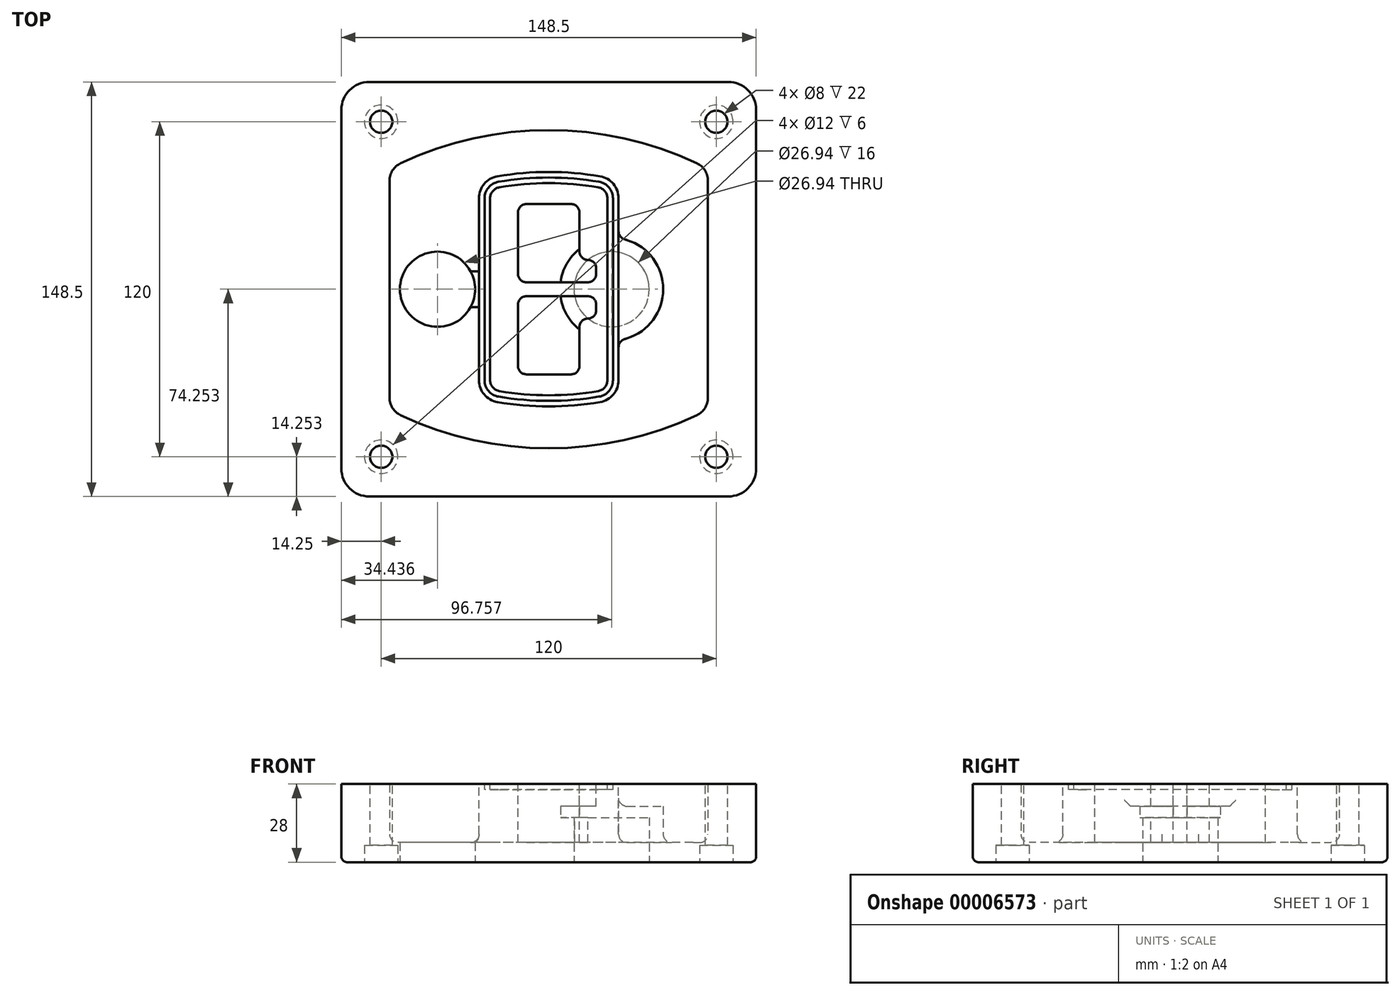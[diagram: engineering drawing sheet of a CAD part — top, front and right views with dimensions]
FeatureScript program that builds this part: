
annotation { "Feature Type Name" : "Feature", "Feature Type Description" : "" }
export const myFeature = defineFeature(function(context is Context, id is Id, definition is map)
    precondition{}
    {
        {
            var Q0;
            Q0=qCreatedBy(makeId("Top.planeOp"),FACE);
            var sketch = newSketch(context, id + "F0", { "sketchPlane" : qUnion([Q0])});
            skPoint(sketch, "E0.rect.middle", {"position": v(0, 0) * mm});
            skLineSegment(sketch, "E1.bottom", {"start": v(24.05, 28.38) * mm, "end": v(152.55, 28.38) * mm});
            skLineSegment(sketch, "E1.top", {"start": v(24.05, 176.88) * mm, "end": v(152.55, 176.88) * mm});
            skLineSegment(sketch, "E1.left", {"start": v(14.05, 38.38) * mm, "end": v(14.05, 166.88) * mm});
            skLineSegment(sketch, "E1.right", {"start": v(162.55, 38.38) * mm, "end": v(162.55, 166.88) * mm});
            skLineSegment(sketch, "E2", {"start": v(14.05, 176.88) * mm, "end": v(162.55, 28.38) * mm, "construction": true});
            skLineSegment(sketch, "E3", {"start": v(162.55, 176.88) * mm, "end": v(14.05, 28.38) * mm, "construction": true});
            skCircle(sketch, "E4", {"center": v(28.3, 162.63) * mm, "radius": 4 * mm});
            skCircle(sketch, "E5", {"center": v(148.3, 162.63) * mm, "radius": 4 * mm});
            skCircle(sketch, "E6", {"center": v(148.3, 42.63) * mm, "radius": 4 * mm});
            skCircle(sketch, "E7", {"center": v(28.3, 42.63) * mm, "radius": 4 * mm});
            skLineSegment(sketch, "E8", {"start": v(28.3, 162.63) * mm, "end": v(148.3, 162.63) * mm, "construction": true});
            skLineSegment(sketch, "E9", {"start": v(148.3, 162.63) * mm, "end": v(148.3, 42.63) * mm, "construction": true});
            skLineSegment(sketch, "E10", {"start": v(148.3, 42.63) * mm, "end": v(28.3, 42.63) * mm, "construction": true});
            skLineSegment(sketch, "E11", {"start": v(28.3, 42.63) * mm, "end": v(28.3, 162.63) * mm, "construction": true});
            skLineSegment(sketch, "E12", {"start": v(28.3, 141.46) * mm, "end": v(28.3, 63.8) * mm});
            skLineSegment(sketch, "E13", {"start": v(148.3, 141.46) * mm, "end": v(148.3, 63.8) * mm});
            skArc(sketch, "E14", {"start": v(142.56, 150.51) * mm, "mid": v(88.3, 162.63) * mm, "end": v(34.04, 150.51) * mm});
            skArc(sketch, "E15", {"start": v(34.04, 54.75) * mm, "mid": v(88.3, 42.63) * mm, "end": v(142.56, 54.75) * mm});
            skLineSegment(sketch, "E16", {"start": v(28.3, 102.63) * mm, "end": v(148.3, 102.63) * mm, "construction": true});
            skPoint(sketch, "E17.visualSharp", {"position": v(28.3, 57.63) * mm});
            skArc(sketch, "E17.filletArc", {"start": v(28.3, 63.8) * mm, "mid": v(29.86, 58.44) * mm, "end": v(34.04, 54.75) * mm});
            skPoint(sketch, "E18.visualSharp", {"position": v(28.3, 147.63) * mm});
            skArc(sketch, "E18.filletArc", {"start": v(34.04, 150.51) * mm, "mid": v(29.86, 146.82) * mm, "end": v(28.3, 141.46) * mm});
            skPoint(sketch, "E19.visualSharp", {"position": v(148.3, 147.63) * mm});
            skArc(sketch, "E19.filletArc", {"start": v(148.3, 141.46) * mm, "mid": v(146.74, 146.82) * mm, "end": v(142.56, 150.51) * mm});
            skPoint(sketch, "E20.visualSharp", {"position": v(148.3, 57.63) * mm});
            skArc(sketch, "E20.filletArc", {"start": v(142.56, 54.75) * mm, "mid": v(146.74, 58.44) * mm, "end": v(148.3, 63.8) * mm});
            skPoint(sketch, "E21.visualSharp", {"position": v(14.05, 176.88) * mm});
            skArc(sketch, "E21.filletArc", {"start": v(24.05, 176.88) * mm, "mid": v(16.98, 173.95) * mm, "end": v(14.05, 166.88) * mm});
            skPoint(sketch, "E22.visualSharp", {"position": v(162.55, 176.88) * mm});
            skArc(sketch, "E22.filletArc", {"start": v(162.55, 166.88) * mm, "mid": v(159.62, 173.95) * mm, "end": v(152.55, 176.88) * mm});
            skPoint(sketch, "E23.visualSharp", {"position": v(162.55, 28.38) * mm});
            skArc(sketch, "E23.filletArc", {"start": v(152.55, 28.38) * mm, "mid": v(159.62, 31.31) * mm, "end": v(162.55, 38.38) * mm});
            skPoint(sketch, "E24.visualSharp", {"position": v(14.05, 28.38) * mm});
            skArc(sketch, "E24.filletArc", {"start": v(14.05, 38.38) * mm, "mid": v(16.98, 31.31) * mm, "end": v(24.05, 28.38) * mm});
            skArc(sketch, "E25.0", {"start": v(145.3, 141.46) * mm, "mid": v(144.2, 145.22) * mm, "end": v(141.28, 147.8) * mm});
            skLineSegment(sketch, "E25.1", {"start": v(145.3, 141.46) * mm, "end": v(145.3, 63.8) * mm});
            skArc(sketch, "E25.2", {"start": v(141.28, 57.47) * mm, "mid": v(144.2, 60.05) * mm, "end": v(145.3, 63.8) * mm});
            skArc(sketch, "E25.3", {"start": v(35.32, 57.47) * mm, "mid": v(88.3, 45.63) * mm, "end": v(141.28, 57.47) * mm});
            skArc(sketch, "E25.4", {"start": v(31.3, 63.8) * mm, "mid": v(32.4, 60.05) * mm, "end": v(35.32, 57.47) * mm});
            skArc(sketch, "E25.5", {"start": v(141.28, 147.8) * mm, "mid": v(88.3, 159.63) * mm, "end": v(35.32, 147.8) * mm});
            skLineSegment(sketch, "E25.6", {"start": v(31.3, 141.46) * mm, "end": v(31.3, 63.8) * mm});
            skArc(sketch, "E25.7", {"start": v(35.32, 147.8) * mm, "mid": v(32.4, 145.22) * mm, "end": v(31.3, 141.46) * mm});
            skArc(sketch, "E26.0", {"start": v(32.34, 154.13) * mm, "mid": v(26.48, 148.97) * mm, "end": v(24.3, 141.46) * mm});
            skArc(sketch, "E26.1", {"start": v(144.26, 154.13) * mm, "mid": v(88.3, 166.63) * mm, "end": v(32.34, 154.13) * mm});
            skArc(sketch, "E26.2", {"start": v(152.3, 141.46) * mm, "mid": v(150.12, 148.97) * mm, "end": v(144.26, 154.13) * mm});
            skLineSegment(sketch, "E26.3", {"start": v(152.3, 141.46) * mm, "end": v(152.3, 63.8) * mm});
            skArc(sketch, "E26.4", {"start": v(144.26, 51.13) * mm, "mid": v(150.12, 56.3) * mm, "end": v(152.3, 63.8) * mm});
            skLineSegment(sketch, "E26.5", {"start": v(24.3, 141.46) * mm, "end": v(24.3, 63.8) * mm});
            skArc(sketch, "E26.6", {"start": v(32.34, 51.13) * mm, "mid": v(88.3, 38.63) * mm, "end": v(144.26, 51.13) * mm});
            skArc(sketch, "E26.7", {"start": v(24.3, 63.8) * mm, "mid": v(26.48, 56.3) * mm, "end": v(32.34, 51.13) * mm});
            skSolve(sketch);
        }
        {
            var Q0;
            Q0=makeQuery(id+"F0.imprint","IMPRINT",FACE,{"disambiguationData":[TD([[makeQuery(id+"F0.imprint","IMPRINT",EDGE,{"derivedFrom":sQuery(id+"F0.wireOp",EDGE,"E1.bottom")}),1.0]])]});
            var Q1;
            Q1=makeQuery(id+"F0.imprint","IMPRINT",FACE,{"disambiguationData":[TD([[makeQuery(id+"F0.imprint","IMPRINT",EDGE,{"derivedFrom":sQuery(id+"F0.wireOp",EDGE,"E12")}),1.0]])]});
            var Q2;
            Q2=makeQuery(id+"F0.imprint","IMPRINT",FACE,{"disambiguationData":[TD([[makeQuery(id+"F0.imprint","IMPRINT",EDGE,{"derivedFrom":sQuery(id+"F0.wireOp",EDGE,"E25.0")}),1.0]])]});
            var Q3;
            Q3=makeQuery(id+"F0.imprint","IMPRINT",FACE,{"disambiguationData":[TD([[makeQuery(id+"F0.imprint","IMPRINT",EDGE,{"derivedFrom":sQuery(id+"F0.wireOp",EDGE,"E12")}),-1.0]])]});
            extrude(context, id + "F1", {"entities" : qUnion([Q0, Q1, Q2, Q3]), "oppositeDirection" : true, "depth" : 25 * mm});
        }
        {
            var Q0;
            Q0=makeQuery(id+"F0.imprint","IMPRINT",FACE,{"disambiguationData":[TD([[makeQuery(id+"F0.imprint","IMPRINT",EDGE,{"derivedFrom":sQuery(id+"F0.wireOp",EDGE,"E12")}),1.0]])]});
            extrude(context, id + "F2", {"entities" : qUnion([Q0]), "operationType" : NewBodyOperationType.ADD, "depth" : 3 * mm});
        }
        {
            var Q0;
            Q0=makeQuery(id+"F0.imprint","IMPRINT",FACE,{"disambiguationData":[TD([[makeQuery(id+"F0.imprint","IMPRINT",EDGE,{"derivedFrom":sQuery(id+"F0.wireOp",EDGE,"E25.0")}),1.0]])]});
            extrude(context, id + "F3", {"entities" : qUnion([Q0]), "operationType" : NewBodyOperationType.REMOVE, "oppositeDirection" : true, "depth" : 18 * mm});
        }
        {
            var Q0;
            Q0=makeQuery(id+"F2.opExtrude","CAP_FACE",FACE,{"disambiguationData":[OSD([sQuery(id+"F0.wireOp",EDGE,"E12"),sQuery(id+"F0.wireOp",EDGE,"E13"),sQuery(id+"F0.wireOp",EDGE,"E14"),sQuery(id+"F0.wireOp",EDGE,"E15"),sQuery(id+"F0.wireOp",EDGE,"E17.filletArc"),sQuery(id+"F0.wireOp",EDGE,"E18.filletArc"),sQuery(id+"F0.wireOp",EDGE,"E19.filletArc"),sQuery(id+"F0.wireOp",EDGE,"E20.filletArc"),sQuery(id+"F0.wireOp",EDGE,"E25.0"),sQuery(id+"F0.wireOp",EDGE,"E25.1"),sQuery(id+"F0.wireOp",EDGE,"E25.2"),sQuery(id+"F0.wireOp",EDGE,"E25.3"),sQuery(id+"F0.wireOp",EDGE,"E25.4"),sQuery(id+"F0.wireOp",EDGE,"E25.5"),sQuery(id+"F0.wireOp",EDGE,"E25.6"),sQuery(id+"F0.wireOp",EDGE,"E25.7")])],"isStart":false});
            var sketch = newSketch(context, id + "F4", { "sketchPlane" : qUnion([Q0])});
            skArc(sketch, "E27.0", {"start": v(69.96, 62.18) * mm, "mid": v(88.3, 60.63) * mm, "end": v(106.64, 62.18) * mm});
            skArc(sketch, "E28.0", {"start": v(106.64, 143.09) * mm, "mid": v(88.3, 144.63) * mm, "end": v(69.96, 143.09) * mm});
            skLineSegment(sketch, "E29", {"start": v(63.3, 135.2) * mm, "end": v(63.3, 70.07) * mm});
            skLineSegment(sketch, "E30", {"start": v(113.3, 135.2) * mm, "end": v(113.3, 70.07) * mm});
            skLineSegment(sketch, "E31", {"start": v(63.3, 141.74) * mm, "end": v(113.3, 141.74) * mm, "construction": true});
            skLineSegment(sketch, "E32", {"start": v(63.3, 63.52) * mm, "end": v(113.3, 63.52) * mm, "construction": true});
            skPoint(sketch, "E33.visualSharp", {"position": v(63.3, 141.74) * mm});
            skArc(sketch, "E33.filletArc", {"start": v(69.96, 143.09) * mm, "mid": v(65.19, 140.36) * mm, "end": v(63.3, 135.2) * mm});
            skPoint(sketch, "E34.visualSharp", {"position": v(113.3, 141.74) * mm});
            skArc(sketch, "E34.filletArc", {"start": v(113.3, 135.2) * mm, "mid": v(111.41, 140.36) * mm, "end": v(106.64, 143.09) * mm});
            skPoint(sketch, "E35.visualSharp", {"position": v(113.3, 63.52) * mm});
            skArc(sketch, "E35.filletArc", {"start": v(106.64, 62.18) * mm, "mid": v(111.41, 64.9) * mm, "end": v(113.3, 70.07) * mm});
            skPoint(sketch, "E36.visualSharp", {"position": v(63.3, 63.52) * mm});
            skArc(sketch, "E36.filletArc", {"start": v(63.3, 70.07) * mm, "mid": v(65.19, 64.9) * mm, "end": v(69.96, 62.18) * mm});
            skArc(sketch, "E37.0", {"start": v(141.28, 147.8) * mm, "mid": v(88.3, 159.63) * mm, "end": v(35.32, 147.8) * mm});
            skArc(sketch, "E37.1", {"start": v(35.32, 147.8) * mm, "mid": v(32.4, 145.22) * mm, "end": v(31.3, 141.46) * mm});
            skLineSegment(sketch, "E37.2", {"start": v(31.3, 141.46) * mm, "end": v(31.3, 63.8) * mm});
            skArc(sketch, "E37.3", {"start": v(31.3, 63.8) * mm, "mid": v(32.4, 60.05) * mm, "end": v(35.32, 57.47) * mm});
            skArc(sketch, "E37.4", {"start": v(35.32, 57.47) * mm, "mid": v(88.3, 45.63) * mm, "end": v(141.28, 57.47) * mm});
            skArc(sketch, "E37.5", {"start": v(141.28, 57.47) * mm, "mid": v(144.2, 60.05) * mm, "end": v(145.3, 63.8) * mm});
            skLineSegment(sketch, "E37.6", {"start": v(145.3, 141.46) * mm, "end": v(145.3, 63.8) * mm});
            skArc(sketch, "E37.7", {"start": v(145.3, 141.46) * mm, "mid": v(144.2, 145.22) * mm, "end": v(141.28, 147.8) * mm});
            skLineSegment(sketch, "E38.0", {"start": v(111.3, 135.2) * mm, "end": v(111.3, 70.07) * mm});
            skArc(sketch, "E38.1", {"start": v(106.3, 64.15) * mm, "mid": v(109.88, 66.2) * mm, "end": v(111.3, 70.07) * mm});
            skArc(sketch, "E38.2", {"start": v(70.3, 64.15) * mm, "mid": v(88.3, 62.63) * mm, "end": v(106.3, 64.15) * mm});
            skArc(sketch, "E38.3", {"start": v(65.3, 70.07) * mm, "mid": v(66.72, 66.2) * mm, "end": v(70.3, 64.15) * mm});
            skLineSegment(sketch, "E38.4", {"start": v(65.3, 135.2) * mm, "end": v(65.3, 70.07) * mm});
            skArc(sketch, "E38.5", {"start": v(111.3, 135.2) * mm, "mid": v(109.88, 139.07) * mm, "end": v(106.3, 141.11) * mm});
            skArc(sketch, "E38.6", {"start": v(70.3, 141.11) * mm, "mid": v(66.72, 139.07) * mm, "end": v(65.3, 135.2) * mm});
            skArc(sketch, "E38.7", {"start": v(106.3, 141.11) * mm, "mid": v(88.3, 142.63) * mm, "end": v(70.3, 141.11) * mm});
            skArc(sketch, "E39.0", {"start": v(109.3, 135.2) * mm, "mid": v(108.36, 137.78) * mm, "end": v(105.97, 139.14) * mm});
            skLineSegment(sketch, "E39.1", {"start": v(109.3, 135.2) * mm, "end": v(109.3, 70.07) * mm});
            skArc(sketch, "E39.2", {"start": v(105.97, 66.12) * mm, "mid": v(108.36, 67.49) * mm, "end": v(109.3, 70.07) * mm});
            skArc(sketch, "E39.3", {"start": v(70.63, 66.12) * mm, "mid": v(88.3, 64.63) * mm, "end": v(105.97, 66.12) * mm});
            skArc(sketch, "E39.4", {"start": v(67.3, 70.07) * mm, "mid": v(68.24, 67.49) * mm, "end": v(70.63, 66.12) * mm});
            skArc(sketch, "E39.5", {"start": v(105.97, 139.14) * mm, "mid": v(88.3, 140.63) * mm, "end": v(70.63, 139.14) * mm});
            skLineSegment(sketch, "E39.6", {"start": v(67.3, 135.2) * mm, "end": v(67.3, 70.07) * mm});
            skArc(sketch, "E39.7", {"start": v(70.63, 139.14) * mm, "mid": v(68.24, 137.78) * mm, "end": v(67.3, 135.2) * mm});
            skLineSegment(sketch, "E40", {"start": v(63.3, 102.63) * mm, "end": v(113.3, 102.63) * mm, "construction": true});
            skLineSegment(sketch, "E41", {"start": v(77.3, 108.13) * mm, "end": v(77.3, 130.13) * mm});
            skLineSegment(sketch, "E42", {"start": v(80.3, 133.13) * mm, "end": v(96.3, 133.13) * mm});
            skLineSegment(sketch, "E43", {"start": v(99.3, 130.13) * mm, "end": v(99.3, 116.13) * mm});
            skLineSegment(sketch, "E44", {"start": v(102.3, 113.13) * mm, "end": v(102.3, 113.13) * mm});
            skLineSegment(sketch, "E45", {"start": v(105.3, 110.13) * mm, "end": v(105.3, 108.13) * mm});
            skLineSegment(sketch, "E46", {"start": v(102.3, 105.13) * mm, "end": v(80.3, 105.13) * mm});
            skPoint(sketch, "E47.visualSharp", {"position": v(77.3, 133.13) * mm});
            skArc(sketch, "E47.filletArc", {"start": v(80.3, 133.13) * mm, "mid": v(78.18, 132.25) * mm, "end": v(77.3, 130.13) * mm});
            skPoint(sketch, "E48.visualSharp", {"position": v(99.3, 133.13) * mm});
            skArc(sketch, "E48.filletArc", {"start": v(99.3, 130.13) * mm, "mid": v(98.42, 132.25) * mm, "end": v(96.3, 133.13) * mm});
            skPoint(sketch, "E49.visualSharp", {"position": v(99.3, 113.13) * mm});
            skArc(sketch, "E49.filletArc", {"start": v(99.3, 116.13) * mm, "mid": v(100.18, 114.01) * mm, "end": v(102.3, 113.13) * mm});
            skPoint(sketch, "E50.visualSharp", {"position": v(105.3, 113.13) * mm});
            skArc(sketch, "E50.filletArc", {"start": v(105.3, 110.13) * mm, "mid": v(104.42, 112.25) * mm, "end": v(102.3, 113.13) * mm});
            skPoint(sketch, "E51.visualSharp", {"position": v(105.3, 105.13) * mm});
            skArc(sketch, "E51.filletArc", {"start": v(102.3, 105.13) * mm, "mid": v(104.42, 106.01) * mm, "end": v(105.3, 108.13) * mm});
            skPoint(sketch, "E52.visualSharp", {"position": v(77.3, 105.13) * mm});
            skArc(sketch, "E52.filletArc", {"start": v(77.3, 108.13) * mm, "mid": v(78.18, 106.01) * mm, "end": v(80.3, 105.13) * mm});
            skLineSegment(sketch, "E53.0.MirrorCS", {"start": v(102.3, 100.13) * mm, "end": v(80.3, 100.13) * mm});
            skArc(sketch, "E54.0.MirrorCS", {"start": v(77.3, 97.13) * mm, "mid": v(78.18, 99.25) * mm, "end": v(80.3, 100.13) * mm});
            skLineSegment(sketch, "E55.0.MirrorCS", {"start": v(77.3, 97.13) * mm, "end": v(77.3, 75.13) * mm});
            skArc(sketch, "E56.0.MirrorCS", {"start": v(80.3, 72.13) * mm, "mid": v(78.18, 73.01) * mm, "end": v(77.3, 75.13) * mm});
            skLineSegment(sketch, "E57.0.MirrorCS", {"start": v(80.3, 72.13) * mm, "end": v(96.3, 72.13) * mm});
            skArc(sketch, "E58.0.MirrorCS", {"start": v(99.3, 75.13) * mm, "mid": v(98.42, 73.01) * mm, "end": v(96.3, 72.13) * mm});
            skLineSegment(sketch, "E59.0.MirrorCS", {"start": v(99.3, 75.13) * mm, "end": v(99.3, 89.13) * mm});
            skArc(sketch, "E60.0.MirrorCS", {"start": v(99.3, 89.13) * mm, "mid": v(100.18, 91.25) * mm, "end": v(102.3, 92.13) * mm});
            skArc(sketch, "E61.0.MirrorCS", {"start": v(105.3, 95.13) * mm, "mid": v(104.42, 93.01) * mm, "end": v(102.3, 92.13) * mm});
            skLineSegment(sketch, "E62.0.MirrorCS", {"start": v(105.3, 95.13) * mm, "end": v(105.3, 97.13) * mm});
            skArc(sketch, "E63.0.MirrorCS", {"start": v(102.3, 100.13) * mm, "mid": v(104.42, 99.25) * mm, "end": v(105.3, 97.13) * mm});
            skSolve(sketch);
        }
        {
            var Q0;
            Q0=makeQuery(id+"F4.imprint","IMPRINT",FACE,{"disambiguationData":[TD([[makeQuery(id+"F4.imprint","IMPRINT",EDGE,{"derivedFrom":sQuery(id+"F4.wireOp",EDGE,"E27.0")}),1.0]])]});
            var Q1;
            Q1=makeQuery(id+"F4.imprint","IMPRINT",FACE,{"disambiguationData":[TD([[makeQuery(id+"F4.imprint","IMPRINT",EDGE,{"derivedFrom":sQuery(id+"F4.wireOp",EDGE,"E38.0")}),-1.0]])]});
            var Q2;
            Q2=makeQuery(id+"F4.imprint","IMPRINT",FACE,{"disambiguationData":[TD([[makeQuery(id+"F4.imprint","IMPRINT",EDGE,{"derivedFrom":sQuery(id+"F4.wireOp",EDGE,"E39.0")}),1.0]])]});
            extrude(context, id + "F5", {"entities" : qUnion([Q0, Q1, Q2]), "operationType" : NewBodyOperationType.ADD, "endBound" : BoundingType.UP_TO_NEXT, "oppositeDirection" : true, "depth" : 25 * mm});
        }
        {
            var Q0;
            Q0=makeQuery(id+"F4.imprint","IMPRINT",FACE,{"disambiguationData":[TD([[makeQuery(id+"F4.imprint","IMPRINT",EDGE,{"derivedFrom":sQuery(id+"F4.wireOp",EDGE,"E38.0")}),-1.0]])]});
            extrude(context, id + "F6", {"entities" : qUnion([Q0]), "operationType" : NewBodyOperationType.REMOVE, "oppositeDirection" : true, "depth" : 2 * mm});
        }
        {
            var Q0;
            Q0=makeQuery(id+"F1.opExtrude","CAP_FACE",FACE,{"disambiguationData":[OSD([sQuery(id+"F0.wireOp",EDGE,"E1.bottom"),sQuery(id+"F0.wireOp",EDGE,"E1.top"),sQuery(id+"F0.wireOp",EDGE,"E1.left"),sQuery(id+"F0.wireOp",EDGE,"E1.right"),sQuery(id+"F0.wireOp",EDGE,"E4"),sQuery(id+"F0.wireOp",EDGE,"E5"),sQuery(id+"F0.wireOp",EDGE,"E6"),sQuery(id+"F0.wireOp",EDGE,"E7"),sQuery(id+"F0.wireOp",EDGE,"E21.filletArc"),sQuery(id+"F0.wireOp",EDGE,"E22.filletArc"),sQuery(id+"F0.wireOp",EDGE,"E23.filletArc"),sQuery(id+"F0.wireOp",EDGE,"E24.filletArc")])],"isStart":false});
            var sketch = newSketch(context, id + "F7", { "sketchPlane" : qUnion([Q0])});
            skCircle(sketch, "E64", {"center": v(110.8, -102.63) * mm, "radius": 13.47 * mm});
            skCircle(sketch, "E65", {"center": v(48.49, -102.63) * mm, "radius": 13.47 * mm});
            skLineSegment(sketch, "E66", {"start": v(162.55, -102.63) * mm, "end": v(14.05, -102.63) * mm});
            skCircle(sketch, "E67", {"center": v(110.8, -102.63) * mm, "radius": 18.47 * mm});
            skCircle(sketch, "E68", {"center": v(148.3, -162.63) * mm, "radius": 6 * mm});
            skCircle(sketch, "E69", {"center": v(28.3, -162.63) * mm, "radius": 6 * mm});
            skCircle(sketch, "E70", {"center": v(28.3, -42.63) * mm, "radius": 6 * mm});
            skCircle(sketch, "E71", {"center": v(148.3, -42.63) * mm, "radius": 6 * mm});
            skSolve(sketch);
        }
        {
            var Q0;
            {var subQ1=sQuery(id+"F7.wireOp",EDGE,"E66");var subQ4=sQuery(id+"F7.wireOp",EDGE,"E64");var subQ6=makeQuery(id+"F7.imprint","INTERSECT",VERTEX,{"disambiguationData":[OD(0.0)],"derivedFrom":[subQ4,subQ1]});Q0=makeQuery(id+"F7.imprint","IMPRINT",FACE,{"disambiguationData":[TD([[makeQuery(id+"F7.imprint","IMPRINT",EDGE,{"disambiguationData":[TD([[subQ6,-1.0]])],"derivedFrom":subQ4}),-1.0]])]});}
            var Q1;
            {var subQ0=sQuery(id+"F7.wireOp",EDGE,"E66");var subQ1=sQuery(id+"F7.wireOp",EDGE,"E64");var subQ3=makeQuery(id+"F7.imprint","INTERSECT",VERTEX,{"disambiguationData":[OD(0.0)],"derivedFrom":[subQ1,subQ0]});Q1=makeQuery(id+"F7.imprint","IMPRINT",FACE,{"disambiguationData":[TD([[makeQuery(id+"F7.imprint","IMPRINT",EDGE,{"disambiguationData":[TD([[subQ3,-1.0]])],"derivedFrom":subQ1}),1.0]])]});}
            var Q2;
            {var subQ0=sQuery(id+"F7.wireOp",EDGE,"E66");var subQ1=sQuery(id+"F7.wireOp",EDGE,"E64");var subQ3=makeQuery(id+"F7.imprint","INTERSECT",VERTEX,{"disambiguationData":[OD(0.0)],"derivedFrom":[subQ1,subQ0]});Q2=makeQuery(id+"F7.imprint","IMPRINT",FACE,{"disambiguationData":[TD([[makeQuery(id+"F7.imprint","IMPRINT",EDGE,{"disambiguationData":[TD([[subQ3,1.0]])],"derivedFrom":subQ1}),1.0]])]});}
            var Q3;
            {var subQ1=sQuery(id+"F7.wireOp",EDGE,"E66");var subQ4=sQuery(id+"F7.wireOp",EDGE,"E64");var subQ6=makeQuery(id+"F7.imprint","INTERSECT",VERTEX,{"disambiguationData":[OD(0.0)],"derivedFrom":[subQ4,subQ1]});Q3=makeQuery(id+"F7.imprint","IMPRINT",FACE,{"disambiguationData":[TD([[makeQuery(id+"F7.imprint","IMPRINT",EDGE,{"disambiguationData":[TD([[subQ6,1.0]])],"derivedFrom":subQ4}),-1.0]])]});}
            extrude(context, id + "F8", {"entities" : qUnion([Q0, Q1, Q2, Q3]), "operationType" : NewBodyOperationType.ADD, "oppositeDirection" : true, "depth" : 20 * mm});
        }
        {
            var Q0;
            {var subQ0=sQuery(id+"F7.wireOp",EDGE,"E66");var subQ1=sQuery(id+"F7.wireOp",EDGE,"E64");var subQ3=makeQuery(id+"F7.imprint","INTERSECT",VERTEX,{"disambiguationData":[OD(0.0)],"derivedFrom":[subQ1,subQ0]});Q0=makeQuery(id+"F7.imprint","IMPRINT",FACE,{"disambiguationData":[TD([[makeQuery(id+"F7.imprint","IMPRINT",EDGE,{"disambiguationData":[TD([[subQ3,-1.0]])],"derivedFrom":subQ1}),1.0]])]});}
            var Q1;
            {var subQ0=sQuery(id+"F7.wireOp",EDGE,"E66");var subQ1=sQuery(id+"F7.wireOp",EDGE,"E64");var subQ3=makeQuery(id+"F7.imprint","INTERSECT",VERTEX,{"disambiguationData":[OD(0.0)],"derivedFrom":[subQ1,subQ0]});Q1=makeQuery(id+"F7.imprint","IMPRINT",FACE,{"disambiguationData":[TD([[makeQuery(id+"F7.imprint","IMPRINT",EDGE,{"disambiguationData":[TD([[subQ3,1.0]])],"derivedFrom":subQ1}),1.0]])]});}
            extrude(context, id + "F9", {"entities" : qUnion([Q0, Q1]), "operationType" : NewBodyOperationType.REMOVE, "oppositeDirection" : true, "depth" : 16 * mm});
        }
        {
            var Q0;
            {var subQ0=sQuery(id+"F7.wireOp",EDGE,"E66");var subQ1=sQuery(id+"F7.wireOp",EDGE,"E65");var subQ3=makeQuery(id+"F7.imprint","INTERSECT",VERTEX,{"disambiguationData":[OD(0.0)],"derivedFrom":[subQ1,subQ0]});Q0=makeQuery(id+"F7.imprint","IMPRINT",FACE,{"disambiguationData":[TD([[makeQuery(id+"F7.imprint","IMPRINT",EDGE,{"disambiguationData":[TD([[subQ3,-1.0]])],"derivedFrom":subQ1}),1.0]])]});}
            var Q1;
            {var subQ0=sQuery(id+"F7.wireOp",EDGE,"E66");var subQ1=sQuery(id+"F7.wireOp",EDGE,"E65");var subQ3=makeQuery(id+"F7.imprint","INTERSECT",VERTEX,{"disambiguationData":[OD(0.0)],"derivedFrom":[subQ1,subQ0]});Q1=makeQuery(id+"F7.imprint","IMPRINT",FACE,{"disambiguationData":[TD([[makeQuery(id+"F7.imprint","IMPRINT",EDGE,{"disambiguationData":[TD([[subQ3,1.0]])],"derivedFrom":subQ1}),1.0]])]});}
            extrude(context, id + "F10", {"entities" : qUnion([Q0, Q1]), "operationType" : NewBodyOperationType.REMOVE, "oppositeDirection" : true, "depth" : 25 * mm});
        }
        {
            var Q0;
            Q0=makeQuery(id+"F7.imprint","IMPRINT",FACE,{"disambiguationData":[TD([[makeQuery(id+"F7.imprint","IMPRINT",EDGE,{"derivedFrom":sQuery(id+"F7.wireOp",EDGE,"E68")}),1.0]])]});
            var Q1;
            Q1=makeQuery(id+"F7.imprint","IMPRINT",FACE,{"disambiguationData":[TD([[makeQuery(id+"F7.imprint","IMPRINT",EDGE,{"derivedFrom":makeQuery(id+"F1.opExtrude","CAP_EDGE",EDGE,{"disambiguationData":[OSD([sQuery(id+"F0.wireOp",EDGE,"E5")])],"isStart":false})}),-1.0]])]});
            var Q2;
            Q2=makeQuery(id+"F7.imprint","IMPRINT",FACE,{"disambiguationData":[TD([[makeQuery(id+"F7.imprint","IMPRINT",EDGE,{"derivedFrom":sQuery(id+"F7.wireOp",EDGE,"E69")}),1.0]])]});
            var Q3;
            Q3=makeQuery(id+"F7.imprint","IMPRINT",FACE,{"disambiguationData":[TD([[makeQuery(id+"F7.imprint","IMPRINT",EDGE,{"derivedFrom":makeQuery(id+"F1.opExtrude","CAP_EDGE",EDGE,{"disambiguationData":[OSD([sQuery(id+"F0.wireOp",EDGE,"E4")])],"isStart":false})}),-1.0]])]});
            var Q4;
            Q4=makeQuery(id+"F7.imprint","IMPRINT",FACE,{"disambiguationData":[TD([[makeQuery(id+"F7.imprint","IMPRINT",EDGE,{"derivedFrom":sQuery(id+"F7.wireOp",EDGE,"E70")}),1.0]])]});
            var Q5;
            Q5=makeQuery(id+"F7.imprint","IMPRINT",FACE,{"disambiguationData":[TD([[makeQuery(id+"F7.imprint","IMPRINT",EDGE,{"derivedFrom":makeQuery(id+"F1.opExtrude","CAP_EDGE",EDGE,{"disambiguationData":[OSD([sQuery(id+"F0.wireOp",EDGE,"E7")])],"isStart":false})}),-1.0]])]});
            var Q6;
            Q6=makeQuery(id+"F7.imprint","IMPRINT",FACE,{"disambiguationData":[TD([[makeQuery(id+"F7.imprint","IMPRINT",EDGE,{"derivedFrom":sQuery(id+"F7.wireOp",EDGE,"E71")}),1.0]])]});
            var Q7;
            Q7=makeQuery(id+"F7.imprint","IMPRINT",FACE,{"disambiguationData":[TD([[makeQuery(id+"F7.imprint","IMPRINT",EDGE,{"derivedFrom":makeQuery(id+"F1.opExtrude","CAP_EDGE",EDGE,{"disambiguationData":[OSD([sQuery(id+"F0.wireOp",EDGE,"E6")])],"isStart":false})}),-1.0]])]});
            extrude(context, id + "F11", {"entities" : qUnion([Q0, Q1, Q2, Q3, Q4, Q5, Q6, Q7]), "operationType" : NewBodyOperationType.REMOVE, "oppositeDirection" : true, "depth" : 6 * mm});
        }
        {
            var Q0;
            Q0=makeQuery(id+"F9.boolean.opBoolean","COPY",FACE,{"derivedFrom":makeQuery(id+"F9.opExtrude","CAP_FACE",FACE,{"disambiguationData":[OSD([sQuery(id+"F7.wireOp",EDGE,"E64")])],"isStart":false})});
            var sketch = newSketch(context, id + "F12", { "sketchPlane" : qUnion([Q0])});
            skArc(sketch, "E72.0", {"start": v(99.3, -88.19) * mm, "mid": v(94.75, -93.5) * mm, "end": v(92.5, -100.13) * mm});
            skArc(sketch, "E72.1", {"start": v(92.5, -105.13) * mm, "mid": v(94.75, -111.76) * mm, "end": v(99.3, -117.08) * mm});
            skLineSegment(sketch, "E73", {"start": v(92.5, -105.13) * mm, "end": v(102.3, -105.13) * mm});
            skLineSegment(sketch, "E74.0", {"start": v(102.3, -100.13) * mm, "end": v(92.5, -100.13) * mm});
            skArc(sketch, "E74.1", {"start": v(102.3, -100.13) * mm, "mid": v(104.42, -99.25) * mm, "end": v(105.3, -97.13) * mm});
            skLineSegment(sketch, "E74.2", {"start": v(105.3, -95.13) * mm, "end": v(105.3, -97.13) * mm});
            skArc(sketch, "E74.3", {"start": v(105.3, -95.13) * mm, "mid": v(104.42, -93.01) * mm, "end": v(102.3, -92.13) * mm});
            skArc(sketch, "E74.4", {"start": v(99.3, -89.13) * mm, "mid": v(100.18, -91.25) * mm, "end": v(102.3, -92.13) * mm});
            skLineSegment(sketch, "E74.5", {"start": v(99.3, -88.19) * mm, "end": v(99.3, -89.13) * mm});
            skLineSegment(sketch, "E74.7", {"start": v(102.3, -105.13) * mm, "end": v(92.5, -105.13) * mm});
            skArc(sketch, "E74.8", {"start": v(102.3, -105.13) * mm, "mid": v(104.42, -106.01) * mm, "end": v(105.3, -108.13) * mm});
            skLineSegment(sketch, "E74.9", {"start": v(105.3, -110.13) * mm, "end": v(105.3, -108.13) * mm});
            skArc(sketch, "E74.10", {"start": v(105.3, -110.13) * mm, "mid": v(104.42, -112.25) * mm, "end": v(102.3, -113.13) * mm});
            skArc(sketch, "E74.11", {"start": v(99.3, -116.13) * mm, "mid": v(100.18, -114.01) * mm, "end": v(102.3, -113.13) * mm});
            skLineSegment(sketch, "E74.12", {"start": v(99.3, -117.08) * mm, "end": v(99.3, -116.13) * mm});
            skPoint(sketch, "E75.orphan", {"position": v(99.3, -130.13) * mm});
            skPoint(sketch, "E76.orphan", {"position": v(80.3, -105.13) * mm});
            skPoint(sketch, "E77.orphan", {"position": v(80.3, -100.13) * mm});
            skPoint(sketch, "E78.orphan", {"position": v(99.3, -75.13) * mm});
            skSolve(sketch);
        }
        {
            var Q0;
            {var subQ7=sQuery(id+"F12.wireOp",EDGE,"E72.0");var subQ14=sQuery(id+"F12.wireOp",EDGE,"E72.1");var subQ16=sQuery(id+"F12.wireOp",EDGE,"E74.1");var subQ18=sQuery(id+"F12.wireOp",EDGE,"E74.8");Q0=qUnion([makeQuery(id+"F12.imprint","IMPRINT",FACE,{"disambiguationData":[TD([[makeQuery(id+"F12.imprint","IMPRINT",EDGE,{"derivedFrom":subQ7}),1.0]])]}),makeQuery(id+"F12.imprint","IMPRINT",FACE,{"disambiguationData":[TD([[makeQuery(id+"F12.imprint","IMPRINT",EDGE,{"derivedFrom":subQ14}),1.0]])]}),makeQuery(id+"F12.imprint","IMPRINT",FACE,{"disambiguationData":[TD([[makeQuery(id+"F12.imprint","IMPRINT",EDGE,{"derivedFrom":subQ16}),1.0]])]}),makeQuery(id+"F12.imprint","IMPRINT",FACE,{"disambiguationData":[TD([[makeQuery(id+"F12.imprint","IMPRINT",EDGE,{"derivedFrom":subQ18}),-1.0]])]})]);}
            var Q1;
            Q1=makeQuery(id+"F5.boolean.opBoolean","SPLIT",FACE,{"disambiguationData":[TD([makeQuery(id+"F5.opExtrude","SWEPT_FACE",FACE,{"disambiguationData":[OSD([sQuery(id+"F4.wireOp",EDGE,"E41")])]})])],"derivedFrom":makeQuery(id+"F3.boolean.opBoolean","COPY",FACE,{"derivedFrom":makeQuery(id+"F3.opExtrude","CAP_FACE",FACE,{"disambiguationData":[OSD([sQuery(id+"F0.wireOp",EDGE,"E25.0"),sQuery(id+"F0.wireOp",EDGE,"E25.1"),sQuery(id+"F0.wireOp",EDGE,"E25.2"),sQuery(id+"F0.wireOp",EDGE,"E25.3"),sQuery(id+"F0.wireOp",EDGE,"E25.4"),sQuery(id+"F0.wireOp",EDGE,"E25.5"),sQuery(id+"F0.wireOp",EDGE,"E25.6"),sQuery(id+"F0.wireOp",EDGE,"E25.7")])],"isStart":false})})});
            extrude(context, id + "F13", {"entities" : qUnion([Q0]), "operationType" : NewBodyOperationType.REMOVE, "endBound" : BoundingType.UP_TO_SURFACE, "endBoundEntityFace" : qUnion([Q1]), "depth" : 25 * mm});
        }
        {
            var Q0;
            Q0=makeQuery(id+"F3.boolean.opBoolean","COPY",EDGE,{"derivedFrom":makeQuery(id+"F3.opExtrude","CAP_EDGE",EDGE,{"disambiguationData":[OSD([sQuery(id+"F0.wireOp",EDGE,"E25.6")])],"isStart":false})});
            var Q1;
            Q1=makeQuery(id+"F8.boolean.opBoolean","INTERSECT",EDGE,{"derivedFrom":[makeQuery(id+"F5.opExtrude","SWEPT_FACE",FACE,{"disambiguationData":[OSD([sQuery(id+"F4.wireOp",EDGE,"E30")])]}),makeQuery(id+"F8.opExtrude","CAP_FACE",FACE,{"disambiguationData":[OSD([sQuery(id+"F7.wireOp",EDGE,"E67")])],"isStart":false})]});
            var Q2;
            Q2=makeQuery(id+"F8.boolean.opBoolean","INTERSECT",EDGE,{"disambiguationData":[OD(1.0)],"derivedFrom":[makeQuery(id+"F5.opExtrude","SWEPT_FACE",FACE,{"disambiguationData":[OSD([sQuery(id+"F4.wireOp",EDGE,"E30")])]}),makeQuery(id+"F8.opExtrude","SWEPT_FACE",FACE,{"disambiguationData":[OSD([sQuery(id+"F7.wireOp",EDGE,"E67")])]})]});
            var Q3;
            {var subQ0=sQuery(id+"F4.wireOp",EDGE,"E30");Q3=makeQuery(id+"F8.boolean.opBoolean","SPLIT",EDGE,{"disambiguationData":[TD([makeQuery(id+"F5.opExtrude","SWEPT_FACE",FACE,{"disambiguationData":[OSD([sQuery(id+"F4.wireOp",EDGE,"E35.filletArc")])]})])],"derivedFrom":makeQuery(id+"F5.opExtrude","CAP_EDGE",EDGE,{"disambiguationData":[OSD([subQ0])],"isStart":false})});}
            var Q4;
            {var subQ0=sQuery(id+"F0.wireOp",EDGE,"E25.7");var subQ1=sQuery(id+"F0.wireOp",EDGE,"E25.1");var subQ2=sQuery(id+"F0.wireOp",EDGE,"E25.6");var subQ3=sQuery(id+"F0.wireOp",EDGE,"E25.5");var subQ4=sQuery(id+"F0.wireOp",EDGE,"E25.4");var subQ5=sQuery(id+"F0.wireOp",EDGE,"E25.0");var subQ6=sQuery(id+"F0.wireOp",EDGE,"E25.2");var subQ7=sQuery(id+"F0.wireOp",EDGE,"E25.3");Q4=makeQuery(id+"F8.boolean.opBoolean","INTERSECT",EDGE,{"derivedFrom":[makeQuery(id+"F5.boolean.opBoolean","SPLIT",FACE,{"disambiguationData":[TD([makeQuery(id+"F2.opExtrude","SWEPT_FACE",FACE,{"disambiguationData":[OSD([subQ5])]})])],"derivedFrom":makeQuery(id+"F3.boolean.opBoolean","COPY",FACE,{"derivedFrom":makeQuery(id+"F3.opExtrude","CAP_FACE",FACE,{"disambiguationData":[OSD([subQ5,subQ1,subQ6,subQ7,subQ4,subQ3,subQ2,subQ0])],"isStart":false})})}),makeQuery(id+"F8.opExtrude","SWEPT_FACE",FACE,{"disambiguationData":[OSD([sQuery(id+"F7.wireOp",EDGE,"E67")])]})]});}
            var Q5;
            Q5=makeQuery(id+"F8.boolean.opBoolean","INTERSECT",EDGE,{"disambiguationData":[OD(0.0)],"derivedFrom":[makeQuery(id+"F5.opExtrude","SWEPT_FACE",FACE,{"disambiguationData":[OSD([sQuery(id+"F4.wireOp",EDGE,"E30")])]}),makeQuery(id+"F8.opExtrude","SWEPT_FACE",FACE,{"disambiguationData":[OSD([sQuery(id+"F7.wireOp",EDGE,"E67")])]})]});
            fillet(context, id + "F14", {"entities" : qUnion([Q0, Q1, Q2, Q3, Q4, Q5]), "radius" : 3 * mm, "tangentPropagation" : true, "allowEdgeOverflow" : false});
        }
        {
            var Q0;
            Q0=makeQuery(id+"F1.opExtrude","CAP_EDGE",EDGE,{"disambiguationData":[OSD([sQuery(id+"F0.wireOp",EDGE,"E1.bottom")])],"isStart":false});
            fillet(context, id + "F15", {"entities" : qUnion([Q0]), "radius" : 2 * mm, "tangentPropagation" : true, "allowEdgeOverflow" : false});
        }
        {
            var Q0;
            {var subQ0=sQuery(id+"F0.wireOp",EDGE,"E1.bottom");var subQ1=sQuery(id+"F0.wireOp",EDGE,"E1.top");var subQ2=sQuery(id+"F0.wireOp",EDGE,"E1.left");var subQ3=sQuery(id+"F0.wireOp",EDGE,"E1.right");var subQ4=sQuery(id+"F0.wireOp",EDGE,"E4");var subQ5=sQuery(id+"F0.wireOp",EDGE,"E5");var subQ6=sQuery(id+"F0.wireOp",EDGE,"E6");var subQ7=sQuery(id+"F0.wireOp",EDGE,"E7");var subQ8=sQuery(id+"F0.wireOp",EDGE,"E21.filletArc");var subQ9=sQuery(id+"F0.wireOp",EDGE,"E22.filletArc");var subQ10=sQuery(id+"F0.wireOp",EDGE,"E23.filletArc");var subQ11=sQuery(id+"F0.wireOp",EDGE,"E24.filletArc");Q0=makeQuery(id+"F2.boolean.opBoolean","SPLIT",FACE,{"disambiguationData":[TD([makeQuery(id+"F1.opExtrude","SWEPT_FACE",FACE,{"disambiguationData":[OSD([subQ0])]})])],"derivedFrom":makeQuery(id+"F1.opExtrude","CAP_FACE",FACE,{"disambiguationData":[OSD([subQ0,subQ1,subQ2,subQ3,subQ4,subQ5,subQ6,subQ7,subQ8,subQ9,subQ10,subQ11])],"isStart":true})});}
            var sketch = newSketch(context, id + "F16", { "sketchPlane" : qUnion([Q0])});
            skLineSegment(sketch, "E79", {"start": v(88.3, 176.88) * mm, "end": v(88.3, 206.88) * mm, "construction": true});
            skCircle(sketch, "E80", {"center": v(88.3, 206.88) * mm, "radius": 6 * mm});
            skArc(sketch, "E81.0", {"start": v(103.3, 206.88) * mm, "mid": v(88.3, 221.88) * mm, "end": v(73.3, 206.88) * mm});
            skLineSegment(sketch, "E82", {"start": v(73.3, 206.88) * mm, "end": v(73.3, 194.88) * mm});
            skLineSegment(sketch, "E83", {"start": v(103.3, 206.88) * mm, "end": v(103.3, 194.88) * mm});
            skLineSegment(sketch, "E84", {"start": v(103.3, 194.88) * mm, "end": v(121.3, 176.88) * mm});
            skLineSegment(sketch, "E85", {"start": v(73.3, 194.88) * mm, "end": v(55.3, 176.88) * mm});
            skLineSegment(sketch, "E86", {"start": v(14.05, 102.63) * mm, "end": v(162.55, 102.63) * mm, "construction": true});
            skArc(sketch, "E87.5.MirrorCS", {"start": v(73.3, 206.88) * mm, "mid": v(88.3, 221.88) * mm, "end": v(103.3, 206.88) * mm});
            skLineSegment(sketch, "E88.0.MirrorCS", {"start": v(162.55, 102.63) * mm, "end": v(14.05, 102.63) * mm, "construction": true});
            skArc(sketch, "E89.0.MirrorCS", {"start": v(103.3, -1.62) * mm, "mid": v(88.3, -16.62) * mm, "end": v(73.3, -1.62) * mm});
            skCircle(sketch, "E90.0.MirrorC", {"center": v(88.3, -1.62) * mm, "radius": 6 * mm});
            skLineSegment(sketch, "E91.0.MirrorCS", {"start": v(73.3, -1.62) * mm, "end": v(73.3, 10.38) * mm});
            skLineSegment(sketch, "E92.0.MirrorCS", {"start": v(103.3, -1.62) * mm, "end": v(103.3, 10.38) * mm});
            skLineSegment(sketch, "E93.0.MirrorCS", {"start": v(103.3, 10.38) * mm, "end": v(121.3, 28.38) * mm});
            skLineSegment(sketch, "E94.0.MirrorCS", {"start": v(73.3, 10.38) * mm, "end": v(55.3, 28.38) * mm});
            skLineSegment(sketch, "E95.0.MirrorCS", {"start": v(88.3, 28.38) * mm, "end": v(88.3, -1.62) * mm, "construction": true});
            skSolve(sketch);
        }
        {
            var Q0;
            {var subQ2=sQuery(id+"F16.wireOp",EDGE,"E84");Q0=makeQuery(id+"F16.imprint","IMPRINT",FACE,{"disambiguationData":[TD([[makeQuery(id+"F16.imprint","IMPRINT",EDGE,{"derivedFrom":subQ2}),-1.0]])]});}
            var sketch = newSketch(context, id + "F17", { "sketchPlane" : qUnion([Q0])});
            skSolve(sketch);
        }
        {
            var Q0;
            Q0=makeQuery(id+"F16.imprint","IMPRINT",FACE,{"disambiguationData":[TD([[makeQuery(id+"F16.imprint","IMPRINT",EDGE,{"derivedFrom":sQuery(id+"F16.wireOp",EDGE,"E89.0.MirrorCS")}),-1.0]])]});
            var Q1;
            Q1=makeQuery(id+"F16.imprint","IMPRINT",FACE,{"disambiguationData":[TD([[makeQuery(id+"F16.imprint","IMPRINT",EDGE,{"derivedFrom":makeQuery(id+"F1.opExtrude","CAP_EDGE",EDGE,{"disambiguationData":[OSD([sQuery(id+"F0.wireOp",EDGE,"E1.left")])],"isStart":true})}),-1.0]])]});
            var Q2;
            {var subQ2=sQuery(id+"F16.wireOp",EDGE,"E84");Q2=makeQuery(id+"F17.imprint","IMPRINT",FACE,{"disambiguationData":[TD([[makeQuery(id+"F17.imprint","IMPRINT",EDGE,{"derivedFrom":makeQuery(id+"F16.imprint","IMPRINT",EDGE,{"derivedFrom":subQ2})}),-1.0]])]});}
            var Q3;
            Q3=makeQuery(id+"F2.opExtrude","CAP_FACE",FACE,{"disambiguationData":[OSD([sQuery(id+"F0.wireOp",EDGE,"E12"),sQuery(id+"F0.wireOp",EDGE,"E13"),sQuery(id+"F0.wireOp",EDGE,"E14"),sQuery(id+"F0.wireOp",EDGE,"E15"),sQuery(id+"F0.wireOp",EDGE,"E17.filletArc"),sQuery(id+"F0.wireOp",EDGE,"E18.filletArc"),sQuery(id+"F0.wireOp",EDGE,"E19.filletArc"),sQuery(id+"F0.wireOp",EDGE,"E20.filletArc"),sQuery(id+"F0.wireOp",EDGE,"E25.0"),sQuery(id+"F0.wireOp",EDGE,"E25.1"),sQuery(id+"F0.wireOp",EDGE,"E25.2"),sQuery(id+"F0.wireOp",EDGE,"E25.3"),sQuery(id+"F0.wireOp",EDGE,"E25.4"),sQuery(id+"F0.wireOp",EDGE,"E25.5"),sQuery(id+"F0.wireOp",EDGE,"E25.6"),sQuery(id+"F0.wireOp",EDGE,"E25.7")])],"isStart":false});
            extrude(context, id + "F18", {"entities" : qUnion([Q0, Q1, Q2]), "operationType" : NewBodyOperationType.ADD, "endBound" : BoundingType.UP_TO_SURFACE, "endBoundEntityFace" : qUnion([Q3]), "depth" : 25 * mm});
        }
    });
